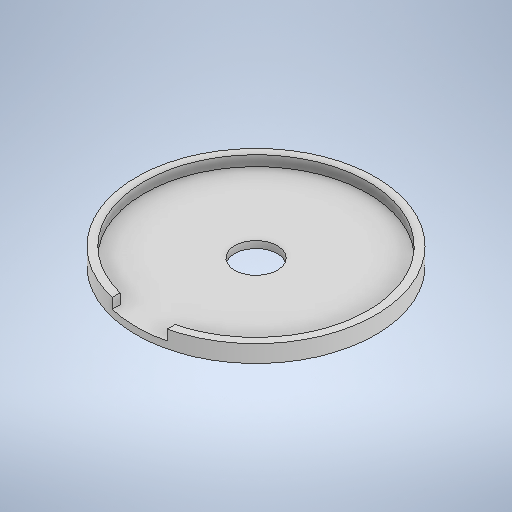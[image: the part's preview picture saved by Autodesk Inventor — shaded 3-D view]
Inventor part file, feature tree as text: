
AUTODESK INVENTOR PART (.ipt)
format: ipt  version: 2025.1 (Build 291241000, 241)  size: 264,704 bytes
history: native  units: mm
features: extrude x4, sketch x4
ambient origin geometry x8: Origin, YZ Plane, XZ Plane, XY Plane, X Axis, Y Axis, Z Axis, Center Point
bodies: Volumenkörper1 (feature_tree)
feature tree (8):
  extrude  "Extrusion1"  Depth=5.0mm TaperAngle=0.0deg
  extrude  "Extrusion2"  Depth=3.0mm TaperAngle=0.0deg
  extrude  "Extrusion3"  TaperAngle=0.0deg  [1 undecoded]
  extrude  "Extrusion4"  Depth=16.0mm
  sketch  "Skizze1"  dims[d0=69.55mm d1=5.0mm d2=0.0mm]
  sketch  "Skizze2"  dims[d3=65.08mm d4=3.0mm d5=0.0mm]
  sketch  "Skizze3"  dims[d6=12.42mm d7=0.0mm d8=0.0mm]
  sketch  "Skizze4"  dims[d9=16.0mm d10=16.0mm d11=10.0mm d12=0.0mm]
note: 1 required parameter value undecoded (feature->parameter linkage not recoverable at this tier; creation-order binding heuristic only, values carry confidence <= 0.55)
